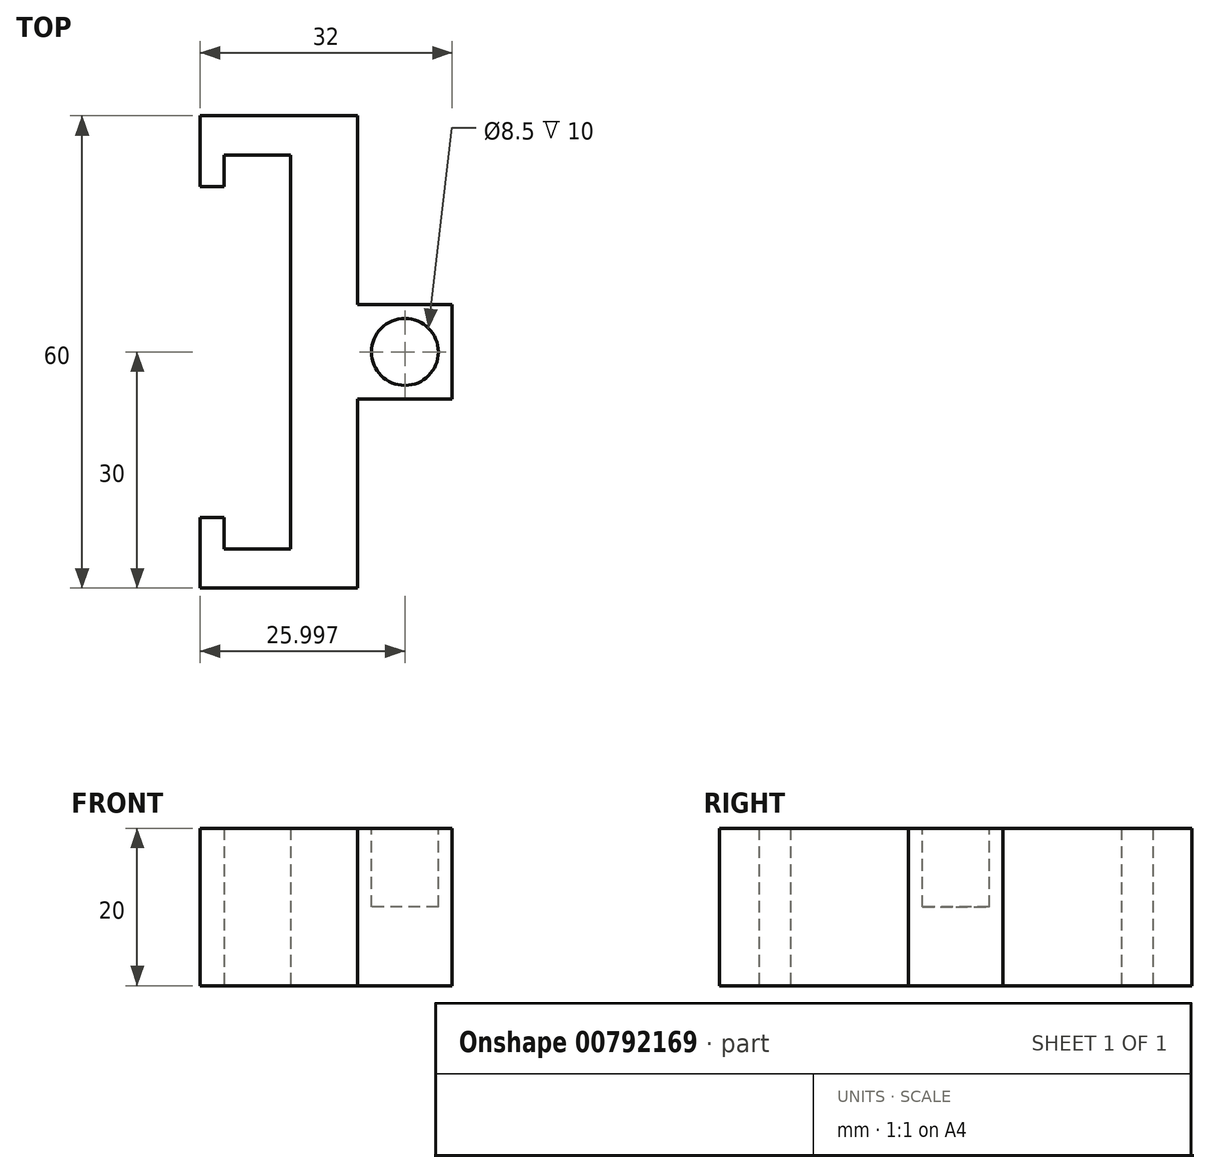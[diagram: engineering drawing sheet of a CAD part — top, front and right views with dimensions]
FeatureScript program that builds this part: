
annotation { "Feature Type Name" : "Feature", "Feature Type Description" : "" }
export const myFeature = defineFeature(function(context is Context, id is Id, definition is map)
    precondition{}
    {
        {
            var Q0;
            Q0=qCreatedBy(makeId("Top.planeOp"),FACE);
            var sketch = newSketch(context, id + "F0", { "sketchPlane" : qUnion([Q0])});
            skLineSegment(sketch, "E0.bottom", {"start": v(0.26, 63.03) * mm, "end": v(20.26, 63.03) * mm});
            skLineSegment(sketch, "E0.top", {"start": v(0.26, 3.03) * mm, "end": v(20.26, 3.03) * mm});
            skLineSegment(sketch, "E1.bottom", {"start": v(20.26, 39.03) * mm, "end": v(32.26, 39.03) * mm});
            skLineSegment(sketch, "E1.top", {"start": v(20.26, 27.03) * mm, "end": v(32.26, 27.03) * mm});
            skLineSegment(sketch, "E1.right", {"start": v(32.26, 39.03) * mm, "end": v(32.26, 27.03) * mm});
            skLineSegment(sketch, "E2.bottom", {"start": v(0.26, 63.03) * mm, "end": v(3.26, 63.03) * mm});
            skLineSegment(sketch, "E2.top", {"start": v(0.26, 54.03) * mm, "end": v(3.26, 54.03) * mm});
            skLineSegment(sketch, "E2.left", {"start": v(0.26, 63.03) * mm, "end": v(0.26, 54.03) * mm});
            skLineSegment(sketch, "E3.bottom", {"start": v(0.26, 3.03) * mm, "end": v(3.26, 3.03) * mm});
            skLineSegment(sketch, "E3.top", {"start": v(0.26, 12.03) * mm, "end": v(3.26, 12.03) * mm});
            skLineSegment(sketch, "E3.left", {"start": v(0.26, 3.03) * mm, "end": v(0.26, 12.03) * mm});
            skLineSegment(sketch, "E4", {"start": v(3.26, 8.03) * mm, "end": v(11.76, 8.03) * mm});
            skLineSegment(sketch, "E5", {"start": v(3.26, 58.03) * mm, "end": v(11.76, 58.03) * mm});
            skLineSegment(sketch, "E6", {"start": v(11.76, 8.03) * mm, "end": v(11.76, 58.03) * mm});
            skLineSegment(sketch, "E7", {"start": v(3.26, 12.03) * mm, "end": v(3.26, 8.03) * mm});
            skLineSegment(sketch, "E8", {"start": v(3.26, 54.03) * mm, "end": v(3.26, 58.03) * mm});
            skLineSegment(sketch, "E9", {"start": v(3.26, 54.03) * mm, "end": v(0.26, 54.03) * mm});
            skLineSegment(sketch, "E10", {"start": v(0.26, 54.03) * mm, "end": v(0.26, 63.03) * mm});
            skLineSegment(sketch, "E11", {"start": v(20.26, 3.03) * mm, "end": v(0.26, 3.03) * mm});
            skLineSegment(sketch, "E12", {"start": v(20.26, 39.03) * mm, "end": v(20.26, 63.03) * mm});
            skLineSegment(sketch, "E13", {"start": v(20.26, 27.03) * mm, "end": v(20.26, 3.03) * mm});
            skLineSegment(sketch, "E14", {"start": v(32.26, 27.03) * mm, "end": v(20.26, 27.03) * mm});
            skSolve(sketch);
        }
        {
            var Q0;
            Q0 = qSketchRegion(id + "F0", true);
            extrude(context, id + "F1", {"entities" : qUnion([Q0]), "depth" : 20 * mm, "offsetDistance" : 25 * mm});
        }
        {
            var Q0;
            Q0=makeQuery(id+"F1.opExtrude","CAP_FACE",FACE,{"disambiguationData":[OSD([sQuery(id+"F0.wireOp",EDGE,"E1.right"),sQuery(id+"F0.wireOp",EDGE,"E4"),sQuery(id+"F0.wireOp",EDGE,"E5"),sQuery(id+"F0.wireOp",EDGE,"E6"),sQuery(id+"F0.wireOp",EDGE,"E8"),sQuery(id+"F0.wireOp",EDGE,"E9"),sQuery(id+"F0.wireOp",EDGE,"E10"),sQuery(id+"F0.wireOp",EDGE,"E0.bottom"),sQuery(id+"F0.wireOp",EDGE,"E11"),sQuery(id+"F0.wireOp",EDGE,"E3.left"),sQuery(id+"F0.wireOp",EDGE,"E3.top"),sQuery(id+"F0.wireOp",EDGE,"E7"),sQuery(id+"F0.wireOp",EDGE,"E12"),sQuery(id+"F0.wireOp",EDGE,"E13"),sQuery(id+"F0.wireOp",EDGE,"E1.bottom"),sQuery(id+"F0.wireOp",EDGE,"E14")])],"isStart":false});
            var sketch = newSketch(context, id + "F2", { "sketchPlane" : qUnion([Q0])});
            skCircle(sketch, "E15", {"center": v(26.26, 33.03) * mm, "radius": 4.25 * mm});
            skSolve(sketch);
        }
        {
            var Q0;
            Q0 = qSketchRegion(id + "F2", true);
            extrude(context, id + "F3", {"entities" : qUnion([Q0]), "operationType" : NewBodyOperationType.REMOVE, "oppositeDirection" : true, "depth" : 10 * mm, "offsetDistance" : 25 * mm});
        }
    });
